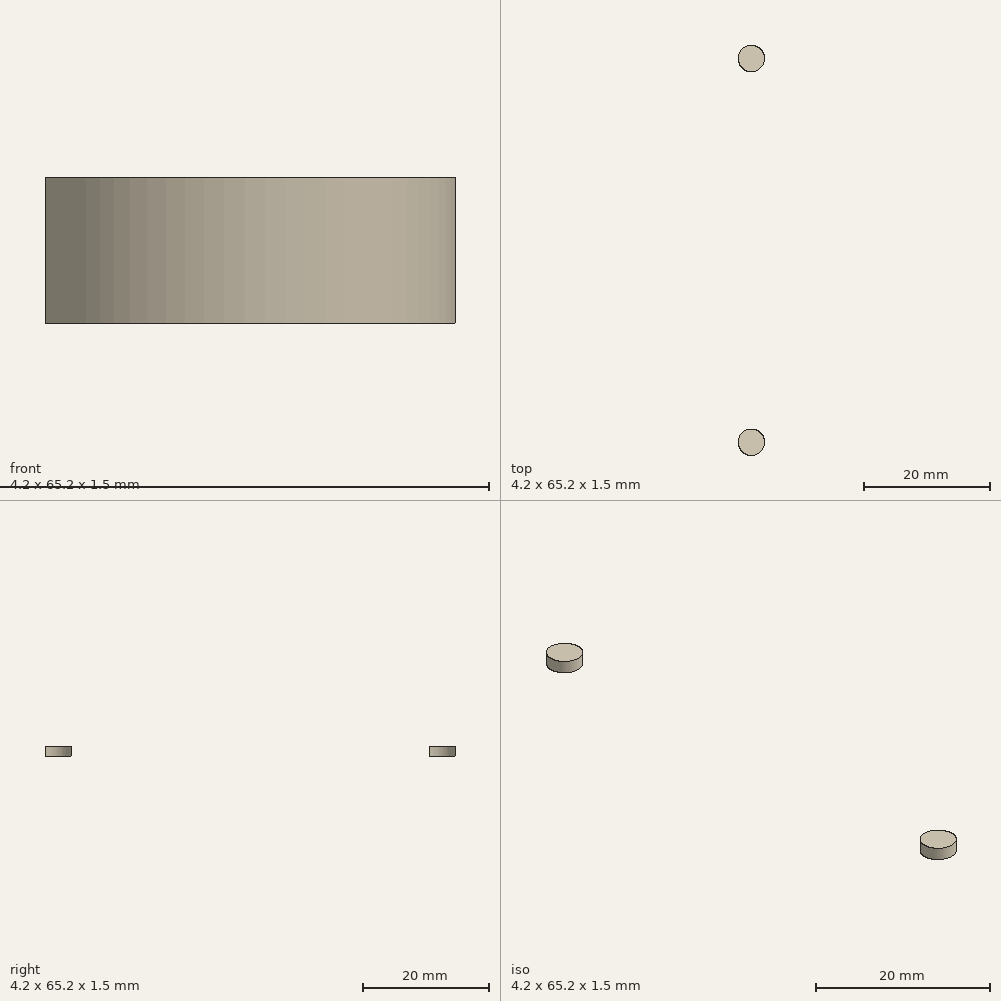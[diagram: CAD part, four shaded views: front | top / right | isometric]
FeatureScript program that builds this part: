
annotation { "Feature Type Name" : "Feature", "Feature Type Description" : "" }
export const myFeature = defineFeature(function(context is Context, id is Id, definition is map)
    precondition{}
    {
        {
            var Q0;
            Q0=qCreatedBy(makeId("Top.planeOp"),FACE);
            var sketch = newSketch(context, id + "F0", { "sketchPlane" : qUnion([Q0])});
            skLineSegment(sketch, "E0.bottom", {"start": v(-89.5, 42) * mm, "end": v(89.5, 42) * mm});
            skLineSegment(sketch, "E0.top", {"start": v(-89.5, -42) * mm, "end": v(89.5, -42) * mm});
            skLineSegment(sketch, "E0.left", {"start": v(-89.5, 42) * mm, "end": v(-89.5, -42) * mm});
            skLineSegment(sketch, "E0.right", {"start": v(89.5, 42) * mm, "end": v(89.5, -42) * mm});
            skLineSegment(sketch, "E1", {"start": v(0, 42) * mm, "end": v(0, -42) * mm, "construction": true});
            skLineSegment(sketch, "E2.bottom", {"start": v(-83, -42) * mm, "end": v(83, -42) * mm});
            skLineSegment(sketch, "E2.top", {"start": v(-82, -55) * mm, "end": v(82, -55) * mm});
            skLineSegment(sketch, "E2.left", {"start": v(-83, -42) * mm, "end": v(-83, -54) * mm});
            skLineSegment(sketch, "E2.right", {"start": v(83, -42) * mm, "end": v(83, -54) * mm});
            skPoint(sketch, "E3.visualSharp", {"position": v(-83, -55) * mm});
            skArc(sketch, "E3.filletArc", {"start": v(-83, -54) * mm, "mid": v(-82.7, -54.7) * mm, "end": v(-82, -55) * mm});
            skPoint(sketch, "E4.visualSharp", {"position": v(83, -55) * mm});
            skArc(sketch, "E4.filletArc", {"start": v(82, -55) * mm, "mid": v(82.7, -54.7) * mm, "end": v(83, -54) * mm});
            skSolve(sketch);
        }
        {
            var Q0;
            Q0=makeQuery(id+"F0.imprint","IMPRINT",FACE,{"disambiguationData":[TD([[makeQuery(id+"F0.imprint","IMPRINT",EDGE,{"derivedFrom":sQuery(id+"F0.wireOp",EDGE,"E2.bottom")}),-1.0]])]});
            var Q1;
            Q1=makeQuery(id+"F0.imprint","IMPRINT",FACE,{"disambiguationData":[TD([[makeQuery(id+"F0.imprint","IMPRINT",EDGE,{"derivedFrom":sQuery(id+"F0.wireOp",EDGE,"E0.bottom")}),-1.0]])]});
            extrude(context, id + "F1", {"entities" : qUnion([Q0, Q1]), "depth" : 1.5 * mm, "offsetDistance" : 25 * mm});
        }
        {
            var Q0;
            Q0=makeQuery(id+"F1.opExtrude","CAP_FACE",FACE,{"disambiguationData":[OSD([sQuery(id+"F0.wireOp",EDGE,"E0.bottom"),sQuery(id+"F0.wireOp",EDGE,"E0.top"),sQuery(id+"F0.wireOp",EDGE,"E0.left"),sQuery(id+"F0.wireOp",EDGE,"E0.right"),sQuery(id+"F0.wireOp",EDGE,"E2.top"),sQuery(id+"F0.wireOp",EDGE,"E2.left"),sQuery(id+"F0.wireOp",EDGE,"E2.right")])],"isStart":false});
            var sketch = newSketch(context, id + "F2", { "sketchPlane" : qUnion([Q0])});
            skLineSegment(sketch, "E5", {"start": v(-89.5, 0) * mm, "end": v(89.5, 0) * mm, "construction": true});
            skCircle(sketch, "E6", {"center": v(-85.5, -38) * mm, "radius": 2.1 * mm});
            skCircle(sketch, "E7", {"center": v(-85.5, 23) * mm, "radius": 2.1 * mm});
            skLineSegment(sketch, "E8", {"start": v(-89.5, 37.5) * mm, "end": v(-85, 42) * mm});
            skLineSegment(sketch, "E9.MirrorCS", {"start": v(-86.5, 128.5) * mm, "end": v(-182, 125.5) * mm, "construction": true});
            skLineSegment(sketch, "E10.direction2", {"start": v(-68, -10) * mm, "end": v(-68, 30.5) * mm, "construction": true});
            skLineSegment(sketch, "E11.MirrorCS", {"start": v(89.5, 37.5) * mm, "end": v(85, 42) * mm});
            skCircle(sketch, "E12.MirrorC", {"center": v(85.5, -38) * mm, "radius": 2.1 * mm});
            skCircle(sketch, "E13.MirrorC", {"center": v(85.5, 23) * mm, "radius": 2.1 * mm});
            skCircle(sketch, "E14", {"center": v(-58, -35) * mm, "radius": 0.6 * mm});
            skCircle(sketch, "E15.0.1.0", {"center": v(-58, -30) * mm, "radius": 0.6 * mm});
            skCircle(sketch, "E15.0.2.0", {"center": v(-58, -25) * mm, "radius": 0.6 * mm});
            skCircle(sketch, "E15.0.3.0", {"center": v(-58, -20) * mm, "radius": 0.6 * mm});
            skCircle(sketch, "E15.0.4.0", {"center": v(-58, -15) * mm, "radius": 0.6 * mm});
            skCircle(sketch, "E15.0.5.0", {"center": v(-58, -10) * mm, "radius": 0.6 * mm});
            skCircle(sketch, "E15.0.6.0", {"center": v(-58, -5) * mm, "radius": 0.6 * mm});
            skCircle(sketch, "E15.0.7.0", {"center": v(-58, 0) * mm, "radius": 0.6 * mm});
            skCircle(sketch, "E15.0.8.0", {"center": v(-58, 5) * mm, "radius": 0.6 * mm});
            skCircle(sketch, "E15.0.9.0", {"center": v(-58, 10) * mm, "radius": 0.6 * mm});
            skCircle(sketch, "E15.1.0.0", {"center": v(-18, -35) * mm, "radius": 0.6 * mm});
            skCircle(sketch, "E15.1.1.0", {"center": v(-18, -30) * mm, "radius": 0.6 * mm});
            skCircle(sketch, "E15.1.2.0", {"center": v(-18, -25) * mm, "radius": 0.6 * mm});
            skCircle(sketch, "E15.1.3.0", {"center": v(-18, -20) * mm, "radius": 0.6 * mm});
            skCircle(sketch, "E15.1.4.0", {"center": v(-18, -15) * mm, "radius": 0.6 * mm});
            skCircle(sketch, "E15.1.5.0", {"center": v(-18, -10) * mm, "radius": 0.6 * mm});
            skCircle(sketch, "E15.1.6.0", {"center": v(-18, -5) * mm, "radius": 0.6 * mm});
            skCircle(sketch, "E15.1.7.0", {"center": v(-18, 0) * mm, "radius": 0.6 * mm});
            skCircle(sketch, "E15.1.8.0", {"center": v(-18, 5) * mm, "radius": 0.6 * mm});
            skCircle(sketch, "E15.1.9.0", {"center": v(-18, 10) * mm, "radius": 0.6 * mm});
            skCircle(sketch, "E15.2.0.0", {"center": v(22, -35) * mm, "radius": 0.6 * mm});
            skCircle(sketch, "E15.2.1.0", {"center": v(22, -30) * mm, "radius": 0.6 * mm});
            skCircle(sketch, "E15.2.2.0", {"center": v(22, -25) * mm, "radius": 0.6 * mm});
            skCircle(sketch, "E15.2.3.0", {"center": v(22, -20) * mm, "radius": 0.6 * mm});
            skCircle(sketch, "E15.2.4.0", {"center": v(22, -15) * mm, "radius": 0.6 * mm});
            skCircle(sketch, "E15.2.5.0", {"center": v(22, -10) * mm, "radius": 0.6 * mm});
            skCircle(sketch, "E15.2.6.0", {"center": v(22, -5) * mm, "radius": 0.6 * mm});
            skCircle(sketch, "E15.2.7.0", {"center": v(22, 0) * mm, "radius": 0.6 * mm});
            skCircle(sketch, "E15.2.8.0", {"center": v(22, 5) * mm, "radius": 0.6 * mm});
            skCircle(sketch, "E15.2.9.0", {"center": v(22, 10) * mm, "radius": 0.6 * mm});
            skCircle(sketch, "E15.3.0.0", {"center": v(62, -35) * mm, "radius": 0.6 * mm});
            skCircle(sketch, "E15.3.1.0", {"center": v(62, -30) * mm, "radius": 0.6 * mm});
            skCircle(sketch, "E15.3.2.0", {"center": v(62, -25) * mm, "radius": 0.6 * mm});
            skCircle(sketch, "E15.3.3.0", {"center": v(62, -20) * mm, "radius": 0.6 * mm});
            skCircle(sketch, "E15.3.4.0", {"center": v(62, -15) * mm, "radius": 0.6 * mm});
            skCircle(sketch, "E15.3.5.0", {"center": v(62, -10) * mm, "radius": 0.6 * mm});
            skCircle(sketch, "E15.3.6.0", {"center": v(62, -5) * mm, "radius": 0.6 * mm});
            skCircle(sketch, "E15.3.7.0", {"center": v(62, 0) * mm, "radius": 0.6 * mm});
            skCircle(sketch, "E15.3.8.0", {"center": v(62, 5) * mm, "radius": 0.6 * mm});
            skCircle(sketch, "E15.3.9.0", {"center": v(62, 10) * mm, "radius": 0.6 * mm});
            skLineSegment(sketch, "E15.direction1", {"start": v(-58, -35) * mm, "end": v(-18, -35) * mm, "construction": true});
            skLineSegment(sketch, "E15.direction2", {"start": v(-58, -35) * mm, "end": v(-58, -30) * mm, "construction": true});
            skSolve(sketch);
        }
        {
            var Q0;
            Q0=makeQuery(id+"F2.imprint","IMPRINT",FACE,{"disambiguationData":[TD([[makeQuery(id+"F2.imprint","IMPRINT",EDGE,{"derivedFrom":sQuery(id+"F2.wireOp",EDGE,"E6")}),1.0]])]});
            var Q1;
            Q1=makeQuery(id+"F2.imprint","IMPRINT",FACE,{"disambiguationData":[TD([[makeQuery(id+"F2.imprint","IMPRINT",EDGE,{"derivedFrom":sQuery(id+"F2.wireOp",EDGE,"qDNhj74A-jXSu-bGPT-YrQy-vhS2jBaaQnZb.bottom")}),-1.0]])]});
            var Q2;
            Q2=makeQuery(id+"F2.imprint","IMPRINT",FACE,{"disambiguationData":[TD([[makeQuery(id+"F2.imprint","IMPRINT",EDGE,{"derivedFrom":sQuery(id+"F2.wireOp",EDGE,"E7")}),1.0]])]});
            var Q3;
            Q3=makeQuery(id+"F2.imprint","IMPRINT",FACE,{"disambiguationData":[TD([[makeQuery(id+"F2.imprint","IMPRINT",EDGE,{"derivedFrom":sQuery(id+"F2.wireOp",EDGE,"ff8556d9-50f2-4100-b515-ed66d0128e750.MirrorC")}),-1.0]])]});
            var Q4;
            Q4=makeQuery(id+"F2.imprint","IMPRINT",FACE,{"disambiguationData":[TD([[makeQuery(id+"F2.imprint","IMPRINT",EDGE,{"derivedFrom":sQuery(id+"F2.wireOp",EDGE,"ff8556d9-50f2-4100-b515-ed66d0128e751.MirrorC")}),-1.0]])]});
            var Q5;
            {var subQ0=sQuery(id+"F2.wireOp",EDGE,"E8");Q5=makeQuery(id+"F2.imprint","IMPRINT",FACE,{"disambiguationData":[TD([[makeQuery(id+"F2.imprint","IMPRINT",EDGE,{"derivedFrom":subQ0}),1.0]])]});}
            var Q6;
            {var subQ0=sQuery(id+"F2.wireOp",EDGE,"67eba9b8-fb38-449f-846f-a493eeb3be840.MirrorCS");Q6=makeQuery(id+"F2.imprint","IMPRINT",FACE,{"disambiguationData":[TD([[makeQuery(id+"F2.imprint","IMPRINT",EDGE,{"derivedFrom":subQ0}),-1.0]])]});}
            var Q7;
            {var subQ0=sQuery(id+"F2.wireOp",EDGE,"gYGCtRZa-QvHC-R8fx-B25b-YyqfIZlm8RDG");var subQ1=makeQuery(id+"F2.imprint","INTERSECT",VERTEX,{"derivedFrom":[subQ0,sQuery(id+"F2.wireOp",EDGE,"7JvcbeNA-OVuB-pVhv-80g0-AVw55zwC8Nza")]});Q7=makeQuery(id+"F2.imprint","IMPRINT",FACE,{"disambiguationData":[TD([[makeQuery(id+"F2.imprint","IMPRINT",EDGE,{"disambiguationData":[TD([[subQ1,-1.0]])],"derivedFrom":subQ0}),1.0]])]});}
            var Q8;
            {var subQ0=sQuery(id+"F2.wireOp",EDGE,"7JvcbeNA-OVuB-pVhv-80g0-AVw55zwC8Nza");Q8=makeQuery(id+"F2.imprint","IMPRINT",FACE,{"disambiguationData":[TD([[makeQuery(id+"F2.imprint","IMPRINT",EDGE,{"derivedFrom":subQ0}),-1.0]])]});}
            var Q9;
            {var subQ0=sQuery(id+"F2.wireOp",EDGE,"vQ1xQvdx-dY70-cDhU-3QJw-tgaTh9b9wvel");var subQ1=makeQuery(id+"F2.imprint","INTERSECT",VERTEX,{"derivedFrom":[subQ0,sQuery(id+"F2.wireOp",EDGE,"7JvcbeNA-OVuB-pVhv-80g0-AVw55zwC8Nza")]});Q9=makeQuery(id+"F2.imprint","IMPRINT",FACE,{"disambiguationData":[TD([[makeQuery(id+"F2.imprint","IMPRINT",EDGE,{"disambiguationData":[TD([[subQ1,-1.0]])],"derivedFrom":subQ0}),1.0]])]});}
            var Q10;
            {var subQ0=sQuery(id+"F2.wireOp",EDGE,"E10.1.0.0");var subQ1=makeQuery(id+"F2.imprint","INTERSECT",VERTEX,{"derivedFrom":[subQ0,sQuery(id+"F2.wireOp",EDGE,"E10.1.0.1")]});Q10=makeQuery(id+"F2.imprint","IMPRINT",FACE,{"disambiguationData":[TD([[makeQuery(id+"F2.imprint","IMPRINT",EDGE,{"disambiguationData":[TD([[subQ1,-1.0]])],"derivedFrom":subQ0}),1.0]])]});}
            var Q11;
            {var subQ0=sQuery(id+"F2.wireOp",EDGE,"E10.1.0.1");Q11=makeQuery(id+"F2.imprint","IMPRINT",FACE,{"disambiguationData":[TD([[makeQuery(id+"F2.imprint","IMPRINT",EDGE,{"derivedFrom":subQ0}),-1.0]])]});}
            var Q12;
            {var subQ0=sQuery(id+"F2.wireOp",EDGE,"E10.1.0.3");var subQ1=makeQuery(id+"F2.imprint","INTERSECT",VERTEX,{"derivedFrom":[sQuery(id+"F2.wireOp",EDGE,"E10.1.0.1"),subQ0]});Q12=makeQuery(id+"F2.imprint","IMPRINT",FACE,{"disambiguationData":[TD([[makeQuery(id+"F2.imprint","IMPRINT",EDGE,{"disambiguationData":[TD([[subQ1,-1.0]])],"derivedFrom":subQ0}),1.0]])]});}
            var Q13;
            {var subQ0=sQuery(id+"F2.wireOp",EDGE,"E10.2.0.0");var subQ1=makeQuery(id+"F2.imprint","INTERSECT",VERTEX,{"derivedFrom":[subQ0,sQuery(id+"F2.wireOp",EDGE,"E10.2.0.1")]});Q13=makeQuery(id+"F2.imprint","IMPRINT",FACE,{"disambiguationData":[TD([[makeQuery(id+"F2.imprint","IMPRINT",EDGE,{"disambiguationData":[TD([[subQ1,-1.0]])],"derivedFrom":subQ0}),1.0]])]});}
            var Q14;
            {var subQ0=sQuery(id+"F2.wireOp",EDGE,"E10.2.0.1");Q14=makeQuery(id+"F2.imprint","IMPRINT",FACE,{"disambiguationData":[TD([[makeQuery(id+"F2.imprint","IMPRINT",EDGE,{"derivedFrom":subQ0}),-1.0]])]});}
            var Q15;
            {var subQ0=sQuery(id+"F2.wireOp",EDGE,"E10.2.0.3");var subQ1=makeQuery(id+"F2.imprint","INTERSECT",VERTEX,{"derivedFrom":[sQuery(id+"F2.wireOp",EDGE,"E10.2.0.1"),subQ0]});Q15=makeQuery(id+"F2.imprint","IMPRINT",FACE,{"disambiguationData":[TD([[makeQuery(id+"F2.imprint","IMPRINT",EDGE,{"disambiguationData":[TD([[subQ1,-1.0]])],"derivedFrom":subQ0}),1.0]])]});}
            var Q16;
            {var subQ0=sQuery(id+"F2.wireOp",EDGE,"E10.3.0.0");var subQ1=makeQuery(id+"F2.imprint","INTERSECT",VERTEX,{"derivedFrom":[subQ0,sQuery(id+"F2.wireOp",EDGE,"E10.3.0.1")]});Q16=makeQuery(id+"F2.imprint","IMPRINT",FACE,{"disambiguationData":[TD([[makeQuery(id+"F2.imprint","IMPRINT",EDGE,{"disambiguationData":[TD([[subQ1,-1.0]])],"derivedFrom":subQ0}),1.0]])]});}
            var Q17;
            {var subQ0=sQuery(id+"F2.wireOp",EDGE,"E10.3.0.1");Q17=makeQuery(id+"F2.imprint","IMPRINT",FACE,{"disambiguationData":[TD([[makeQuery(id+"F2.imprint","IMPRINT",EDGE,{"derivedFrom":subQ0}),-1.0]])]});}
            var Q18;
            {var subQ0=sQuery(id+"F2.wireOp",EDGE,"E10.3.0.3");var subQ1=makeQuery(id+"F2.imprint","INTERSECT",VERTEX,{"derivedFrom":[sQuery(id+"F2.wireOp",EDGE,"E10.3.0.1"),subQ0]});Q18=makeQuery(id+"F2.imprint","IMPRINT",FACE,{"disambiguationData":[TD([[makeQuery(id+"F2.imprint","IMPRINT",EDGE,{"disambiguationData":[TD([[subQ1,-1.0]])],"derivedFrom":subQ0}),1.0]])]});}
            var Q19;
            {var subQ0=sQuery(id+"F2.wireOp",EDGE,"E10.4.0.0");var subQ1=makeQuery(id+"F2.imprint","INTERSECT",VERTEX,{"derivedFrom":[subQ0,sQuery(id+"F2.wireOp",EDGE,"E10.4.0.1")]});Q19=makeQuery(id+"F2.imprint","IMPRINT",FACE,{"disambiguationData":[TD([[makeQuery(id+"F2.imprint","IMPRINT",EDGE,{"disambiguationData":[TD([[subQ1,-1.0]])],"derivedFrom":subQ0}),1.0]])]});}
            var Q20;
            {var subQ0=sQuery(id+"F2.wireOp",EDGE,"E10.4.0.1");Q20=makeQuery(id+"F2.imprint","IMPRINT",FACE,{"disambiguationData":[TD([[makeQuery(id+"F2.imprint","IMPRINT",EDGE,{"derivedFrom":subQ0}),-1.0]])]});}
            var Q21;
            {var subQ0=sQuery(id+"F2.wireOp",EDGE,"E10.4.0.3");var subQ1=makeQuery(id+"F2.imprint","INTERSECT",VERTEX,{"derivedFrom":[sQuery(id+"F2.wireOp",EDGE,"E10.4.0.1"),subQ0]});Q21=makeQuery(id+"F2.imprint","IMPRINT",FACE,{"disambiguationData":[TD([[makeQuery(id+"F2.imprint","IMPRINT",EDGE,{"disambiguationData":[TD([[subQ1,-1.0]])],"derivedFrom":subQ0}),1.0]])]});}
            var Q22;
            {var subQ0=sQuery(id+"F2.wireOp",EDGE,"E10.5.0.0");var subQ1=makeQuery(id+"F2.imprint","INTERSECT",VERTEX,{"derivedFrom":[subQ0,sQuery(id+"F2.wireOp",EDGE,"E10.5.0.1")]});Q22=makeQuery(id+"F2.imprint","IMPRINT",FACE,{"disambiguationData":[TD([[makeQuery(id+"F2.imprint","IMPRINT",EDGE,{"disambiguationData":[TD([[subQ1,-1.0]])],"derivedFrom":subQ0}),1.0]])]});}
            var Q23;
            {var subQ0=sQuery(id+"F2.wireOp",EDGE,"E10.5.0.1");Q23=makeQuery(id+"F2.imprint","IMPRINT",FACE,{"disambiguationData":[TD([[makeQuery(id+"F2.imprint","IMPRINT",EDGE,{"derivedFrom":subQ0}),-1.0]])]});}
            var Q24;
            {var subQ0=sQuery(id+"F2.wireOp",EDGE,"E10.5.0.3");var subQ1=makeQuery(id+"F2.imprint","INTERSECT",VERTEX,{"derivedFrom":[sQuery(id+"F2.wireOp",EDGE,"E10.5.0.1"),subQ0]});Q24=makeQuery(id+"F2.imprint","IMPRINT",FACE,{"disambiguationData":[TD([[makeQuery(id+"F2.imprint","IMPRINT",EDGE,{"disambiguationData":[TD([[subQ1,-1.0]])],"derivedFrom":subQ0}),1.0]])]});}
            var Q25;
            {var subQ0=sQuery(id+"F2.wireOp",EDGE,"E10.5.1.3");var subQ1=makeQuery(id+"F2.imprint","INTERSECT",VERTEX,{"derivedFrom":[sQuery(id+"F2.wireOp",EDGE,"E10.5.1.1"),subQ0]});Q25=makeQuery(id+"F2.imprint","IMPRINT",FACE,{"disambiguationData":[TD([[makeQuery(id+"F2.imprint","IMPRINT",EDGE,{"disambiguationData":[TD([[subQ1,-1.0]])],"derivedFrom":subQ0}),1.0]])]});}
            var Q26;
            {var subQ0=sQuery(id+"F2.wireOp",EDGE,"E10.5.1.1");Q26=makeQuery(id+"F2.imprint","IMPRINT",FACE,{"disambiguationData":[TD([[makeQuery(id+"F2.imprint","IMPRINT",EDGE,{"derivedFrom":subQ0}),-1.0]])]});}
            var Q27;
            {var subQ0=sQuery(id+"F2.wireOp",EDGE,"E10.5.1.0");var subQ1=makeQuery(id+"F2.imprint","INTERSECT",VERTEX,{"derivedFrom":[subQ0,sQuery(id+"F2.wireOp",EDGE,"E10.5.1.1")]});Q27=makeQuery(id+"F2.imprint","IMPRINT",FACE,{"disambiguationData":[TD([[makeQuery(id+"F2.imprint","IMPRINT",EDGE,{"disambiguationData":[TD([[subQ1,-1.0]])],"derivedFrom":subQ0}),1.0]])]});}
            var Q28;
            {var subQ0=sQuery(id+"F2.wireOp",EDGE,"E10.4.1.1");Q28=makeQuery(id+"F2.imprint","IMPRINT",FACE,{"disambiguationData":[TD([[makeQuery(id+"F2.imprint","IMPRINT",EDGE,{"derivedFrom":subQ0}),-1.0]])]});}
            var Q29;
            {var subQ0=sQuery(id+"F2.wireOp",EDGE,"E10.1.1.3");var subQ1=makeQuery(id+"F2.imprint","INTERSECT",VERTEX,{"derivedFrom":[sQuery(id+"F2.wireOp",EDGE,"E10.1.1.1"),subQ0]});Q29=makeQuery(id+"F2.imprint","IMPRINT",FACE,{"disambiguationData":[TD([[makeQuery(id+"F2.imprint","IMPRINT",EDGE,{"disambiguationData":[TD([[subQ1,-1.0]])],"derivedFrom":subQ0}),1.0]])]});}
            var Q30;
            {var subQ0=sQuery(id+"F2.wireOp",EDGE,"E10.1.1.0");var subQ1=makeQuery(id+"F2.imprint","INTERSECT",VERTEX,{"derivedFrom":[subQ0,sQuery(id+"F2.wireOp",EDGE,"E10.1.1.1")]});Q30=makeQuery(id+"F2.imprint","IMPRINT",FACE,{"disambiguationData":[TD([[makeQuery(id+"F2.imprint","IMPRINT",EDGE,{"disambiguationData":[TD([[subQ1,-1.0]])],"derivedFrom":subQ0}),1.0]])]});}
            var Q31;
            {var subQ0=sQuery(id+"F2.wireOp",EDGE,"E10.1.1.1");Q31=makeQuery(id+"F2.imprint","IMPRINT",FACE,{"disambiguationData":[TD([[makeQuery(id+"F2.imprint","IMPRINT",EDGE,{"derivedFrom":subQ0}),-1.0]])]});}
            var Q32;
            {var subQ0=sQuery(id+"F2.wireOp",EDGE,"E10.0.1.0");var subQ1=makeQuery(id+"F2.imprint","INTERSECT",VERTEX,{"derivedFrom":[subQ0,sQuery(id+"F2.wireOp",EDGE,"E10.0.1.1")]});Q32=makeQuery(id+"F2.imprint","IMPRINT",FACE,{"disambiguationData":[TD([[makeQuery(id+"F2.imprint","IMPRINT",EDGE,{"disambiguationData":[TD([[subQ1,-1.0]])],"derivedFrom":subQ0}),1.0]])]});}
            var Q33;
            {var subQ0=sQuery(id+"F2.wireOp",EDGE,"E10.0.1.1");Q33=makeQuery(id+"F2.imprint","IMPRINT",FACE,{"disambiguationData":[TD([[makeQuery(id+"F2.imprint","IMPRINT",EDGE,{"derivedFrom":subQ0}),-1.0]])]});}
            var Q34;
            {var subQ0=sQuery(id+"F2.wireOp",EDGE,"E10.0.1.3");var subQ1=makeQuery(id+"F2.imprint","INTERSECT",VERTEX,{"derivedFrom":[sQuery(id+"F2.wireOp",EDGE,"E10.0.1.1"),subQ0]});Q34=makeQuery(id+"F2.imprint","IMPRINT",FACE,{"disambiguationData":[TD([[makeQuery(id+"F2.imprint","IMPRINT",EDGE,{"disambiguationData":[TD([[subQ1,-1.0]])],"derivedFrom":subQ0}),1.0]])]});}
            var Q35;
            {var subQ0=sQuery(id+"F2.wireOp",EDGE,"E10.2.1.1");Q35=makeQuery(id+"F2.imprint","IMPRINT",FACE,{"disambiguationData":[TD([[makeQuery(id+"F2.imprint","IMPRINT",EDGE,{"derivedFrom":subQ0}),-1.0]])]});}
            var Q36;
            {var subQ0=sQuery(id+"F2.wireOp",EDGE,"E10.2.1.3");var subQ1=makeQuery(id+"F2.imprint","INTERSECT",VERTEX,{"derivedFrom":[sQuery(id+"F2.wireOp",EDGE,"E10.2.1.1"),subQ0]});Q36=makeQuery(id+"F2.imprint","IMPRINT",FACE,{"disambiguationData":[TD([[makeQuery(id+"F2.imprint","IMPRINT",EDGE,{"disambiguationData":[TD([[subQ1,-1.0]])],"derivedFrom":subQ0}),1.0]])]});}
            var Q37;
            {var subQ0=sQuery(id+"F2.wireOp",EDGE,"E10.3.1.3");var subQ1=makeQuery(id+"F2.imprint","INTERSECT",VERTEX,{"derivedFrom":[sQuery(id+"F2.wireOp",EDGE,"E10.3.1.1"),subQ0]});Q37=makeQuery(id+"F2.imprint","IMPRINT",FACE,{"disambiguationData":[TD([[makeQuery(id+"F2.imprint","IMPRINT",EDGE,{"disambiguationData":[TD([[subQ1,-1.0]])],"derivedFrom":subQ0}),1.0]])]});}
            var Q38;
            {var subQ0=sQuery(id+"F2.wireOp",EDGE,"E10.4.1.0");var subQ1=makeQuery(id+"F2.imprint","INTERSECT",VERTEX,{"derivedFrom":[subQ0,sQuery(id+"F2.wireOp",EDGE,"E10.4.1.1")]});Q38=makeQuery(id+"F2.imprint","IMPRINT",FACE,{"disambiguationData":[TD([[makeQuery(id+"F2.imprint","IMPRINT",EDGE,{"disambiguationData":[TD([[subQ1,-1.0]])],"derivedFrom":subQ0}),1.0]])]});}
            var Q39;
            {var subQ0=sQuery(id+"F2.wireOp",EDGE,"E10.2.1.0");var subQ1=makeQuery(id+"F2.imprint","INTERSECT",VERTEX,{"derivedFrom":[subQ0,sQuery(id+"F2.wireOp",EDGE,"E10.2.1.1")]});Q39=makeQuery(id+"F2.imprint","IMPRINT",FACE,{"disambiguationData":[TD([[makeQuery(id+"F2.imprint","IMPRINT",EDGE,{"disambiguationData":[TD([[subQ1,-1.0]])],"derivedFrom":subQ0}),1.0]])]});}
            var Q40;
            {var subQ0=sQuery(id+"F2.wireOp",EDGE,"E10.3.1.0");var subQ1=makeQuery(id+"F2.imprint","INTERSECT",VERTEX,{"derivedFrom":[subQ0,sQuery(id+"F2.wireOp",EDGE,"E10.3.1.1")]});Q40=makeQuery(id+"F2.imprint","IMPRINT",FACE,{"disambiguationData":[TD([[makeQuery(id+"F2.imprint","IMPRINT",EDGE,{"disambiguationData":[TD([[subQ1,-1.0]])],"derivedFrom":subQ0}),1.0]])]});}
            var Q41;
            {var subQ0=sQuery(id+"F2.wireOp",EDGE,"E10.3.1.1");Q41=makeQuery(id+"F2.imprint","IMPRINT",FACE,{"disambiguationData":[TD([[makeQuery(id+"F2.imprint","IMPRINT",EDGE,{"derivedFrom":subQ0}),-1.0]])]});}
            var Q42;
            {var subQ0=sQuery(id+"F2.wireOp",EDGE,"E10.4.1.3");var subQ1=makeQuery(id+"F2.imprint","INTERSECT",VERTEX,{"derivedFrom":[sQuery(id+"F2.wireOp",EDGE,"E10.4.1.1"),subQ0]});Q42=makeQuery(id+"F2.imprint","IMPRINT",FACE,{"disambiguationData":[TD([[makeQuery(id+"F2.imprint","IMPRINT",EDGE,{"disambiguationData":[TD([[subQ1,-1.0]])],"derivedFrom":subQ0}),1.0]])]});}
            var Q43;
            Q43=makeQuery(id+"F2.imprint","IMPRINT",FACE,{"disambiguationData":[TD([[makeQuery(id+"F2.imprint","IMPRINT",EDGE,{"derivedFrom":sQuery(id+"F2.wireOp",EDGE,"E12.MirrorC")}),-1.0]])]});
            var Q44;
            {var subQ0=sQuery(id+"F2.wireOp",EDGE,"E11.MirrorCS");Q44=makeQuery(id+"F2.imprint","IMPRINT",FACE,{"disambiguationData":[TD([[makeQuery(id+"F2.imprint","IMPRINT",EDGE,{"derivedFrom":subQ0}),-1.0]])]});}
            var Q45;
            Q45=makeQuery(id+"F2.imprint","IMPRINT",FACE,{"disambiguationData":[TD([[makeQuery(id+"F2.imprint","IMPRINT",EDGE,{"derivedFrom":sQuery(id+"F2.wireOp",EDGE,"E13.MirrorC")}),-1.0]])]});
            var Q46;
            Q46=makeQuery(id+"F2.imprint","IMPRINT",FACE,{"disambiguationData":[TD([[makeQuery(id+"F2.imprint","IMPRINT",EDGE,{"derivedFrom":sQuery(id+"F2.wireOp",EDGE,"E14")}),1.0]])]});
            var Q47;
            Q47=makeQuery(id+"F2.imprint","IMPRINT",FACE,{"disambiguationData":[TD([[makeQuery(id+"F2.imprint","IMPRINT",EDGE,{"derivedFrom":sQuery(id+"F2.wireOp",EDGE,"E15.0.1.0")}),1.0]])]});
            var Q48;
            Q48=makeQuery(id+"F2.imprint","IMPRINT",FACE,{"disambiguationData":[TD([[makeQuery(id+"F2.imprint","IMPRINT",EDGE,{"derivedFrom":sQuery(id+"F2.wireOp",EDGE,"E15.0.2.0")}),1.0]])]});
            var Q49;
            Q49=makeQuery(id+"F2.imprint","IMPRINT",FACE,{"disambiguationData":[TD([[makeQuery(id+"F2.imprint","IMPRINT",EDGE,{"derivedFrom":sQuery(id+"F2.wireOp",EDGE,"E15.0.3.0")}),1.0]])]});
            var Q50;
            Q50=makeQuery(id+"F2.imprint","IMPRINT",FACE,{"disambiguationData":[TD([[makeQuery(id+"F2.imprint","IMPRINT",EDGE,{"derivedFrom":sQuery(id+"F2.wireOp",EDGE,"E15.0.4.0")}),1.0]])]});
            var Q51;
            Q51=makeQuery(id+"F2.imprint","IMPRINT",FACE,{"disambiguationData":[TD([[makeQuery(id+"F2.imprint","IMPRINT",EDGE,{"derivedFrom":sQuery(id+"F2.wireOp",EDGE,"E15.0.5.0")}),1.0]])]});
            var Q52;
            Q52=makeQuery(id+"F2.imprint","IMPRINT",FACE,{"disambiguationData":[TD([[makeQuery(id+"F2.imprint","IMPRINT",EDGE,{"derivedFrom":sQuery(id+"F2.wireOp",EDGE,"E15.0.6.0")}),1.0]])]});
            var Q53;
            Q53=makeQuery(id+"F2.imprint","IMPRINT",FACE,{"disambiguationData":[TD([[makeQuery(id+"F2.imprint","IMPRINT",EDGE,{"derivedFrom":sQuery(id+"F2.wireOp",EDGE,"E15.0.7.0")}),1.0]])]});
            var Q54;
            Q54=makeQuery(id+"F2.imprint","IMPRINT",FACE,{"disambiguationData":[TD([[makeQuery(id+"F2.imprint","IMPRINT",EDGE,{"derivedFrom":sQuery(id+"F2.wireOp",EDGE,"E15.0.8.0")}),1.0]])]});
            var Q55;
            Q55=makeQuery(id+"F2.imprint","IMPRINT",FACE,{"disambiguationData":[TD([[makeQuery(id+"F2.imprint","IMPRINT",EDGE,{"derivedFrom":sQuery(id+"F2.wireOp",EDGE,"E15.0.9.0")}),1.0]])]});
            var Q56;
            Q56=makeQuery(id+"F2.imprint","IMPRINT",FACE,{"disambiguationData":[TD([[makeQuery(id+"F2.imprint","IMPRINT",EDGE,{"derivedFrom":sQuery(id+"F2.wireOp",EDGE,"E15.1.9.0")}),1.0]])]});
            var Q57;
            Q57=makeQuery(id+"F2.imprint","IMPRINT",FACE,{"disambiguationData":[TD([[makeQuery(id+"F2.imprint","IMPRINT",EDGE,{"derivedFrom":sQuery(id+"F2.wireOp",EDGE,"E15.1.8.0")}),1.0]])]});
            var Q58;
            Q58=makeQuery(id+"F2.imprint","IMPRINT",FACE,{"disambiguationData":[TD([[makeQuery(id+"F2.imprint","IMPRINT",EDGE,{"derivedFrom":sQuery(id+"F2.wireOp",EDGE,"E15.1.7.0")}),1.0]])]});
            var Q59;
            Q59=makeQuery(id+"F2.imprint","IMPRINT",FACE,{"disambiguationData":[TD([[makeQuery(id+"F2.imprint","IMPRINT",EDGE,{"derivedFrom":sQuery(id+"F2.wireOp",EDGE,"E15.1.6.0")}),1.0]])]});
            var Q60;
            Q60=makeQuery(id+"F2.imprint","IMPRINT",FACE,{"disambiguationData":[TD([[makeQuery(id+"F2.imprint","IMPRINT",EDGE,{"derivedFrom":sQuery(id+"F2.wireOp",EDGE,"E15.1.5.0")}),1.0]])]});
            var Q61;
            Q61=makeQuery(id+"F2.imprint","IMPRINT",FACE,{"disambiguationData":[TD([[makeQuery(id+"F2.imprint","IMPRINT",EDGE,{"derivedFrom":sQuery(id+"F2.wireOp",EDGE,"E15.1.4.0")}),1.0]])]});
            var Q62;
            Q62=makeQuery(id+"F2.imprint","IMPRINT",FACE,{"disambiguationData":[TD([[makeQuery(id+"F2.imprint","IMPRINT",EDGE,{"derivedFrom":sQuery(id+"F2.wireOp",EDGE,"E15.1.3.0")}),1.0]])]});
            var Q63;
            Q63=makeQuery(id+"F2.imprint","IMPRINT",FACE,{"disambiguationData":[TD([[makeQuery(id+"F2.imprint","IMPRINT",EDGE,{"derivedFrom":sQuery(id+"F2.wireOp",EDGE,"E15.1.2.0")}),1.0]])]});
            var Q64;
            Q64=makeQuery(id+"F2.imprint","IMPRINT",FACE,{"disambiguationData":[TD([[makeQuery(id+"F2.imprint","IMPRINT",EDGE,{"derivedFrom":sQuery(id+"F2.wireOp",EDGE,"E15.1.1.0")}),1.0]])]});
            var Q65;
            Q65=makeQuery(id+"F2.imprint","IMPRINT",FACE,{"disambiguationData":[TD([[makeQuery(id+"F2.imprint","IMPRINT",EDGE,{"derivedFrom":sQuery(id+"F2.wireOp",EDGE,"E15.1.0.0")}),1.0]])]});
            var Q66;
            Q66=makeQuery(id+"F2.imprint","IMPRINT",FACE,{"disambiguationData":[TD([[makeQuery(id+"F2.imprint","IMPRINT",EDGE,{"derivedFrom":sQuery(id+"F2.wireOp",EDGE,"E15.2.0.0")}),1.0]])]});
            var Q67;
            Q67=makeQuery(id+"F2.imprint","IMPRINT",FACE,{"disambiguationData":[TD([[makeQuery(id+"F2.imprint","IMPRINT",EDGE,{"derivedFrom":sQuery(id+"F2.wireOp",EDGE,"E15.2.1.0")}),1.0]])]});
            var Q68;
            Q68=makeQuery(id+"F2.imprint","IMPRINT",FACE,{"disambiguationData":[TD([[makeQuery(id+"F2.imprint","IMPRINT",EDGE,{"derivedFrom":sQuery(id+"F2.wireOp",EDGE,"E15.2.2.0")}),1.0]])]});
            var Q69;
            Q69=makeQuery(id+"F2.imprint","IMPRINT",FACE,{"disambiguationData":[TD([[makeQuery(id+"F2.imprint","IMPRINT",EDGE,{"derivedFrom":sQuery(id+"F2.wireOp",EDGE,"E15.2.3.0")}),1.0]])]});
            var Q70;
            Q70=makeQuery(id+"F2.imprint","IMPRINT",FACE,{"disambiguationData":[TD([[makeQuery(id+"F2.imprint","IMPRINT",EDGE,{"derivedFrom":sQuery(id+"F2.wireOp",EDGE,"E15.2.4.0")}),1.0]])]});
            var Q71;
            Q71=makeQuery(id+"F2.imprint","IMPRINT",FACE,{"disambiguationData":[TD([[makeQuery(id+"F2.imprint","IMPRINT",EDGE,{"derivedFrom":sQuery(id+"F2.wireOp",EDGE,"E15.2.5.0")}),1.0]])]});
            var Q72;
            Q72=makeQuery(id+"F2.imprint","IMPRINT",FACE,{"disambiguationData":[TD([[makeQuery(id+"F2.imprint","IMPRINT",EDGE,{"derivedFrom":sQuery(id+"F2.wireOp",EDGE,"E15.2.6.0")}),1.0]])]});
            var Q73;
            Q73=makeQuery(id+"F2.imprint","IMPRINT",FACE,{"disambiguationData":[TD([[makeQuery(id+"F2.imprint","IMPRINT",EDGE,{"derivedFrom":sQuery(id+"F2.wireOp",EDGE,"E15.2.7.0")}),1.0]])]});
            var Q74;
            Q74=makeQuery(id+"F2.imprint","IMPRINT",FACE,{"disambiguationData":[TD([[makeQuery(id+"F2.imprint","IMPRINT",EDGE,{"derivedFrom":sQuery(id+"F2.wireOp",EDGE,"E15.2.8.0")}),1.0]])]});
            var Q75;
            Q75=makeQuery(id+"F2.imprint","IMPRINT",FACE,{"disambiguationData":[TD([[makeQuery(id+"F2.imprint","IMPRINT",EDGE,{"derivedFrom":sQuery(id+"F2.wireOp",EDGE,"E15.2.9.0")}),1.0]])]});
            var Q76;
            Q76=makeQuery(id+"F2.imprint","IMPRINT",FACE,{"disambiguationData":[TD([[makeQuery(id+"F2.imprint","IMPRINT",EDGE,{"derivedFrom":sQuery(id+"F2.wireOp",EDGE,"E15.3.9.0")}),1.0]])]});
            var Q77;
            Q77=makeQuery(id+"F2.imprint","IMPRINT",FACE,{"disambiguationData":[TD([[makeQuery(id+"F2.imprint","IMPRINT",EDGE,{"derivedFrom":sQuery(id+"F2.wireOp",EDGE,"E15.3.8.0")}),1.0]])]});
            var Q78;
            Q78=makeQuery(id+"F2.imprint","IMPRINT",FACE,{"disambiguationData":[TD([[makeQuery(id+"F2.imprint","IMPRINT",EDGE,{"derivedFrom":sQuery(id+"F2.wireOp",EDGE,"E15.3.7.0")}),1.0]])]});
            var Q79;
            Q79=makeQuery(id+"F2.imprint","IMPRINT",FACE,{"disambiguationData":[TD([[makeQuery(id+"F2.imprint","IMPRINT",EDGE,{"derivedFrom":sQuery(id+"F2.wireOp",EDGE,"E15.3.6.0")}),1.0]])]});
            var Q80;
            Q80=makeQuery(id+"F2.imprint","IMPRINT",FACE,{"disambiguationData":[TD([[makeQuery(id+"F2.imprint","IMPRINT",EDGE,{"derivedFrom":sQuery(id+"F2.wireOp",EDGE,"E15.3.5.0")}),1.0]])]});
            var Q81;
            Q81=makeQuery(id+"F2.imprint","IMPRINT",FACE,{"disambiguationData":[TD([[makeQuery(id+"F2.imprint","IMPRINT",EDGE,{"derivedFrom":sQuery(id+"F2.wireOp",EDGE,"E15.3.4.0")}),1.0]])]});
            var Q82;
            Q82=makeQuery(id+"F2.imprint","IMPRINT",FACE,{"disambiguationData":[TD([[makeQuery(id+"F2.imprint","IMPRINT",EDGE,{"derivedFrom":sQuery(id+"F2.wireOp",EDGE,"E15.3.3.0")}),1.0]])]});
            var Q83;
            Q83=makeQuery(id+"F2.imprint","IMPRINT",FACE,{"disambiguationData":[TD([[makeQuery(id+"F2.imprint","IMPRINT",EDGE,{"derivedFrom":sQuery(id+"F2.wireOp",EDGE,"E15.3.2.0")}),1.0]])]});
            var Q84;
            Q84=makeQuery(id+"F2.imprint","IMPRINT",FACE,{"disambiguationData":[TD([[makeQuery(id+"F2.imprint","IMPRINT",EDGE,{"derivedFrom":sQuery(id+"F2.wireOp",EDGE,"E15.3.1.0")}),1.0]])]});
            var Q85;
            Q85=makeQuery(id+"F2.imprint","IMPRINT",FACE,{"disambiguationData":[TD([[makeQuery(id+"F2.imprint","IMPRINT",EDGE,{"derivedFrom":sQuery(id+"F2.wireOp",EDGE,"E15.3.0.0")}),1.0]])]});
            extrude(context, id + "F3", {"entities" : qUnion([Q0, Q1, Q2, Q3, Q4, Q5, Q6, Q7, Q8, Q9, Q10, Q11, Q12, Q13, Q14, Q15, Q16, Q17, Q18, Q19, Q20, Q21, Q22, Q23, Q24, Q25, Q26, Q27, Q28, Q29, Q30, Q31, Q32, Q33, Q34, Q35, Q36, Q37, Q38, Q39, Q40, Q41, Q42, Q43, Q44, Q45, Q46, Q47, Q48, Q49, Q50, Q51, Q52, Q53, Q54, Q55, Q56, Q57, Q58, Q59, Q60, Q61, Q62, Q63, Q64, Q65, Q66, Q67, Q68, Q69, Q70, Q71, Q72, Q73, Q74, Q75, Q76, Q77, Q78, Q79, Q80, Q81, Q82, Q83, Q84, Q85]), "operationType" : NewBodyOperationType.REMOVE, "endBound" : BoundingType.THROUGH_ALL, "oppositeDirection" : true, "depth" : 25 * mm, "offsetDistance" : 25 * mm});
        }
    });
